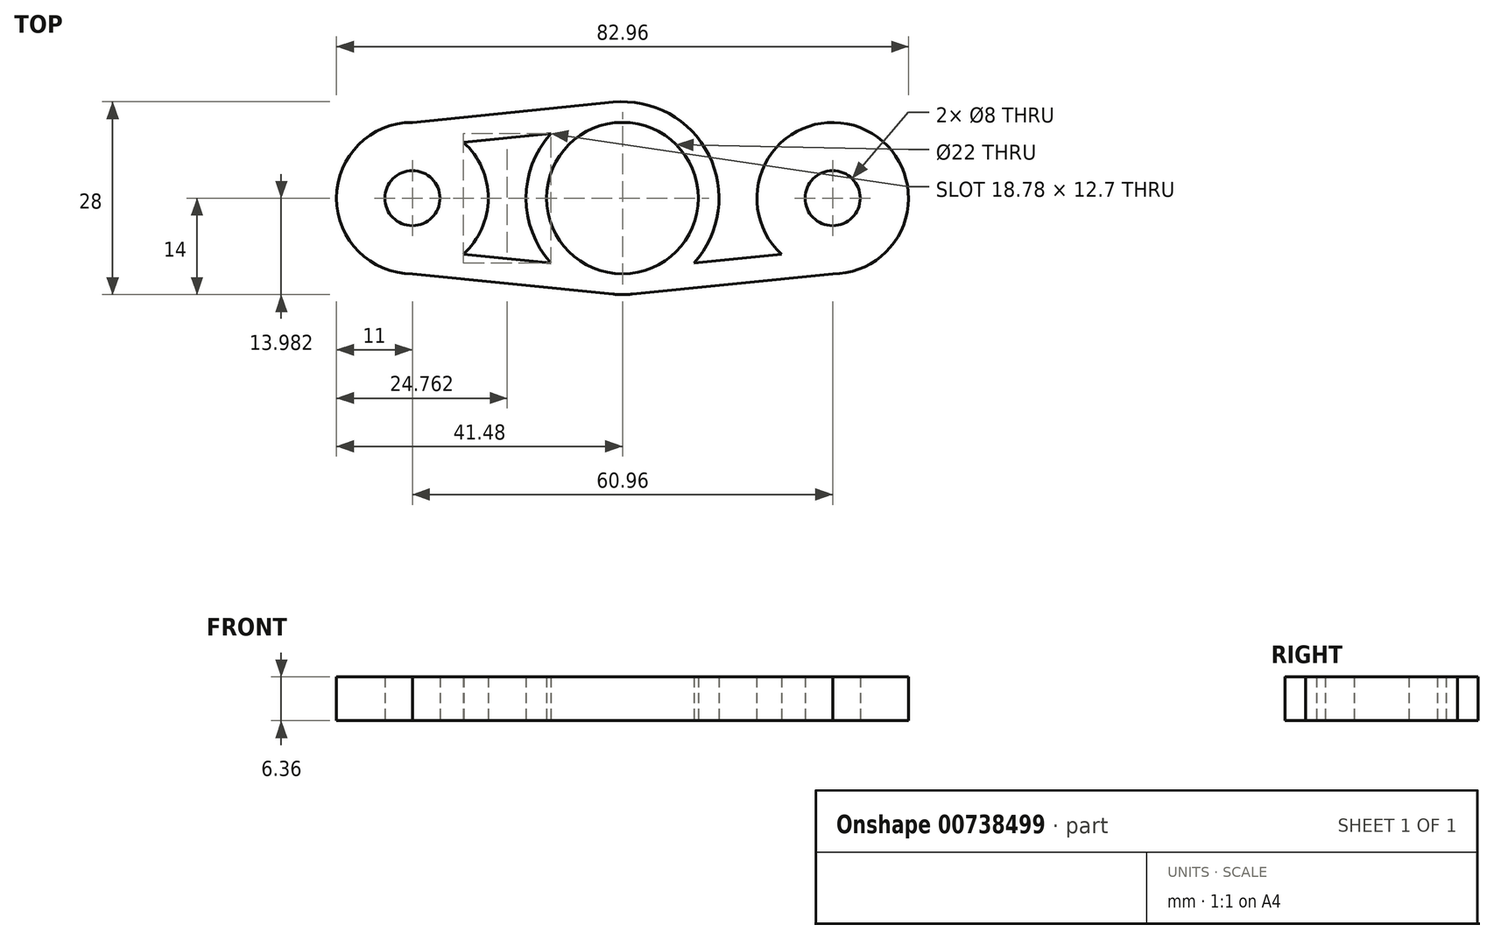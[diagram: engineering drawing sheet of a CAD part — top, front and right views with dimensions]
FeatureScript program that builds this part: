
annotation { "Feature Type Name" : "Feature", "Feature Type Description" : "" }
export const myFeature = defineFeature(function(context is Context, id is Id, definition is map)
    precondition{}
    {
        {
            var Q0;
            Q0=qCreatedBy(makeId("Top.planeOp"),FACE);
            var sketch = newSketch(context, id + "F0", { "sketchPlane" : qUnion([Q0])});
            skCircle(sketch, "E0", {"center": v(0, 0) * mm, "radius": 11 * mm});
            skCircle(sketch, "E1", {"center": v(-30.48, 0) * mm, "radius": 11 * mm});
            skCircle(sketch, "E2", {"center": v(30.48, 0) * mm, "radius": 11 * mm});
            skCircle(sketch, "E3", {"center": v(0, 0) * mm, "radius": 14 * mm});
            skLineSegment(sketch, "E4", {"start": v(-30.48, -11) * mm, "end": v(0, -14.07) * mm});
            skLineSegment(sketch, "E5", {"start": v(0, -14.07) * mm, "end": v(30.48, -11) * mm});
            skLineSegment(sketch, "E6", {"start": v(-30.48, 11) * mm, "end": v(0, 14.07) * mm});
            skLineSegment(sketch, "E7", {"start": v(-23.04, 8.1) * mm, "end": v(-10.4, 9.37) * mm});
            skLineSegment(sketch, "E8", {"start": v(-23.07, -8.13) * mm, "end": v(-10.37, -9.4) * mm});
            skLineSegment(sketch, "E9", {"start": v(10.37, -9.4) * mm, "end": v(23.07, -8.13) * mm});
            skLineSegment(sketch, "E10", {"start": v(30.48, 11) * mm, "end": v(0, 14.07) * mm});
            skLineSegment(sketch, "E11", {"start": v(10.4, 9.37) * mm, "end": v(23.04, 8.1) * mm});
            skLineSegment(sketch, "E12", {"start": v(23.04, 8.1) * mm, "end": v(10.4, 9.37) * mm});
            skCircle(sketch, "E13", {"center": v(-30.48, 0) * mm, "radius": 4 * mm});
            skCircle(sketch, "E14", {"center": v(30.48, 0) * mm, "radius": 4 * mm});
            skSolve(sketch);
        }
        {
            var Q0;
            Q0=makeQuery(id+"F0.imprint","IMPRINT",FACE,{"disambiguationData":[TD([[makeQuery(id+"F0.imprint","IMPRINT",EDGE,{"derivedFrom":sQuery(id+"F0.wireOp",EDGE,"E13")}),-1.0]])]});
            var Q1;
            Q1=makeQuery(id+"F0.imprint","IMPRINT",FACE,{"disambiguationData":[TD([[makeQuery(id+"F0.imprint","IMPRINT",EDGE,{"derivedFrom":sQuery(id+"F0.wireOp",EDGE,"E0")}),-1.0]])]});
            var Q2;
            {var subQ3=sQuery(id+"F0.wireOp",EDGE,"E7");Q2=makeQuery(id+"F0.imprint","IMPRINT",FACE,{"disambiguationData":[TD([[makeQuery(id+"F0.imprint","IMPRINT",EDGE,{"derivedFrom":subQ3}),1.0]])]});}
            var Q3;
            {var subQ3=sQuery(id+"F0.wireOp",EDGE,"E8");Q3=makeQuery(id+"F0.imprint","IMPRINT",FACE,{"disambiguationData":[TD([[makeQuery(id+"F0.imprint","IMPRINT",EDGE,{"derivedFrom":subQ3}),-1.0]])]});}
            var Q4;
            {var subQ3=sQuery(id+"F0.wireOp",EDGE,"E9");Q4=makeQuery(id+"F0.imprint","IMPRINT",FACE,{"disambiguationData":[TD([[makeQuery(id+"F0.imprint","IMPRINT",EDGE,{"derivedFrom":subQ3}),-1.0]])]});}
            var Q5;
            Q5=makeQuery(id+"F0.imprint","IMPRINT",FACE,{"disambiguationData":[TD([[makeQuery(id+"F0.imprint","IMPRINT",EDGE,{"derivedFrom":sQuery(id+"F0.wireOp",EDGE,"E14")}),-1.0]])]});
            var Q6;
            {var subQ3=sQuery(id+"F0.wireOp",EDGE,"E12");Q6=makeQuery(id+"F0.imprint","IMPRINT",FACE,{"disambiguationData":[TD([[makeQuery(id+"F0.imprint","IMPRINT",EDGE,{"derivedFrom":subQ3}),-1.0]])]});}
            extrude(context, id + "F1", {"entities" : qUnion([Q0, Q1, Q2, Q3, Q4, Q5, Q6]), "depth" : 6.35 * mm, "offsetDistance" : 25.4 * mm, "symmetric" : true});
        }
    });
